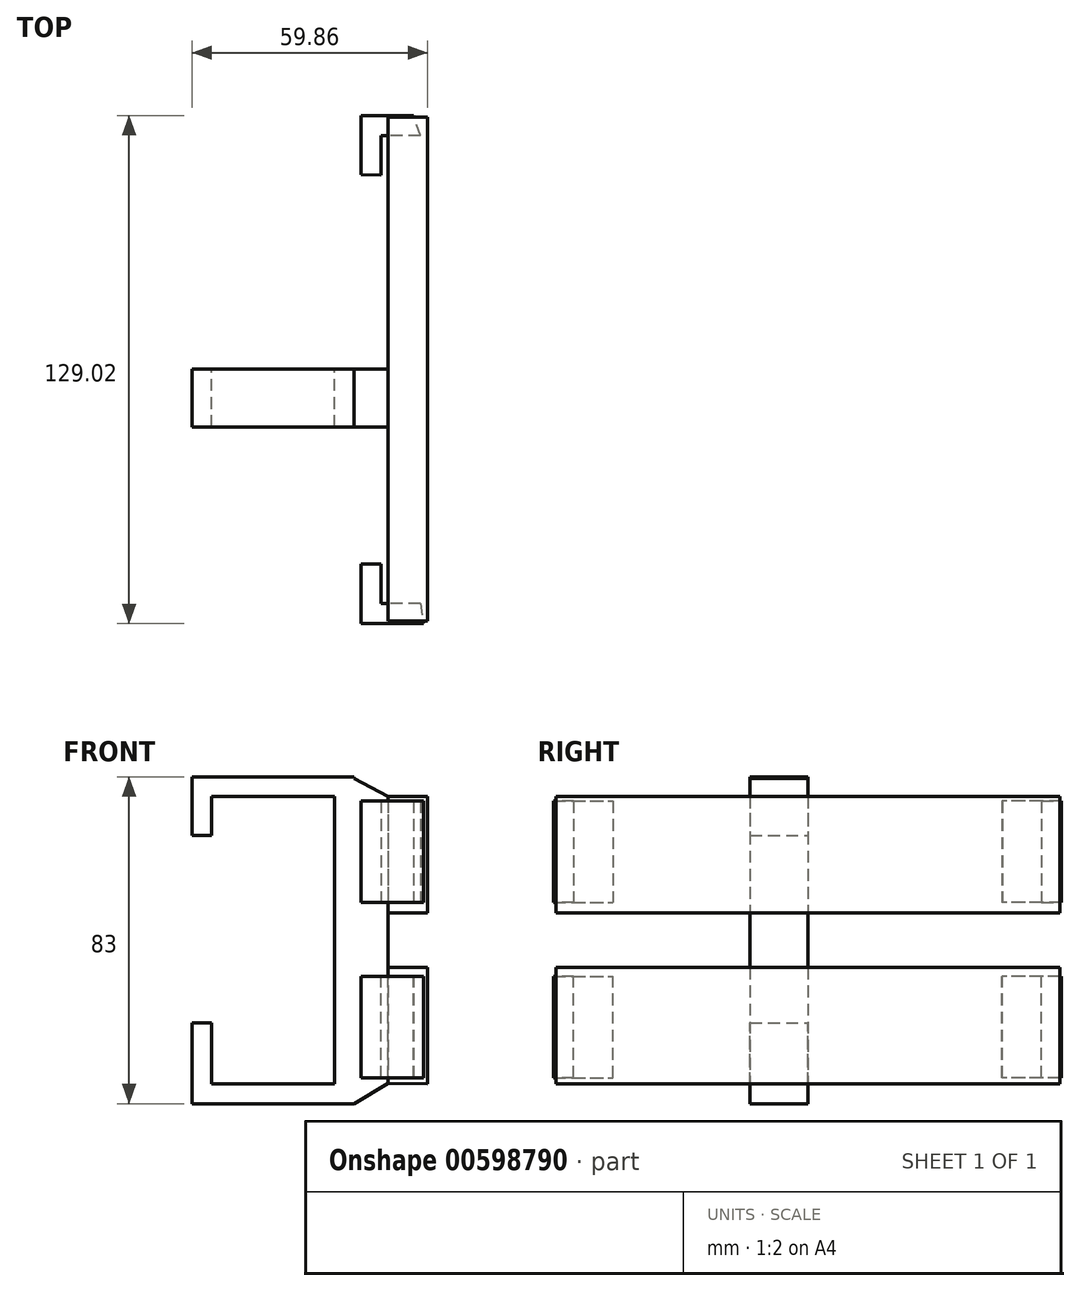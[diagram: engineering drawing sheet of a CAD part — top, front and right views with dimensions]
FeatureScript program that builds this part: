
annotation { "Feature Type Name" : "Feature", "Feature Type Description" : "" }
export const myFeature = defineFeature(function(context is Context, id is Id, definition is map)
    precondition{}
    {
        {
            var Q0;
            Q0=qCreatedBy(makeId("Front.planeOp"),FACE);
            var sketch = newSketch(context, id + "F0", { "sketchPlane" : qUnion([Q0])});
            skLineSegment(sketch, "E0", {"start": v(-93.76, -37.98) * mm, "end": v(-62.56, -37.98) * mm});
            skLineSegment(sketch, "E1", {"start": v(-62.56, -37.98) * mm, "end": v(-62.56, 35.02) * mm});
            skLineSegment(sketch, "E2", {"start": v(-62.56, 35.02) * mm, "end": v(-93.76, 35.02) * mm});
            skLineSegment(sketch, "E3", {"start": v(-93.76, 35.02) * mm, "end": v(-93.76, 25.22) * mm});
            skLineSegment(sketch, "E4", {"start": v(-93.76, -37.98) * mm, "end": v(-93.76, -22.48) * mm});
            skLineSegment(sketch, "E5.0", {"start": v(-98.76, 40.02) * mm, "end": v(-98.76, 25.22) * mm});
            skLineSegment(sketch, "E5.1", {"start": v(-98.76, -42.98) * mm, "end": v(-98.76, -22.48) * mm});
            skLineSegment(sketch, "E5.2", {"start": v(-98.76, -42.98) * mm, "end": v(-57.56, -42.98) * mm});
            skLineSegment(sketch, "E5.3", {"start": v(-57.56, -42.98) * mm, "end": v(-57.56, 40.02) * mm});
            skLineSegment(sketch, "E5.4", {"start": v(-57.56, 40.02) * mm, "end": v(-98.76, 40.02) * mm});
            skLineSegment(sketch, "E6", {"start": v(-93.76, 25.22) * mm, "end": v(-98.76, 25.22) * mm});
            skLineSegment(sketch, "E7", {"start": v(-93.76, -22.48) * mm, "end": v(-98.76, -22.48) * mm});
            skLineSegment(sketch, "E8", {"start": v(-57.56, 35.06) * mm, "end": v(-48.9, 35.06) * mm});
            skLineSegment(sketch, "E9", {"start": v(-48.9, 35.06) * mm, "end": v(-48.9, -37.87) * mm});
            skLineSegment(sketch, "E10", {"start": v(-48.9, -37.87) * mm, "end": v(-57.56, -37.87) * mm});
            skLineSegment(sketch, "E11", {"start": v(-57.94, 39.83) * mm, "end": v(-48.9, 35.06) * mm});
            skLineSegment(sketch, "E12", {"start": v(-48.9, -37.87) * mm, "end": v(-57.56, -42.98) * mm});
            skLineSegment(sketch, "E13", {"start": v(-38.9, 5.52) * mm, "end": v(-38.9, 35.02) * mm});
            skLineSegment(sketch, "E14", {"start": v(-38.9, 35.02) * mm, "end": v(-48.9, 35.06) * mm});
            skLineSegment(sketch, "E15", {"start": v(-48.9, -37.87) * mm, "end": v(-38.9, -37.9) * mm});
            skLineSegment(sketch, "E16", {"start": v(-38.9, -37.9) * mm, "end": v(-38.9, -8.4) * mm});
            skLineSegment(sketch, "E17", {"start": v(-38.9, -8.4) * mm, "end": v(-48.9, -8.37) * mm});
            skPoint(sketch, "E18.start.orphan", {"position": v(-38.9, 3.98) * mm});
            skLineSegment(sketch, "E19", {"start": v(-38.9, 5.52) * mm, "end": v(-48.9, 5.52) * mm});
            skSolve(sketch);
        }
        {
            var Q0;
            {var subQ2=sQuery(id+"F0.wireOp",EDGE,"E10");Q0=makeQuery(id+"F0.imprint","IMPRINT",FACE,{"disambiguationData":[TD([[makeQuery(id+"F0.imprint","IMPRINT",EDGE,{"derivedFrom":subQ2}),1.0]])]});}
            var Q1;
            {var subQ0=sQuery(id+"F0.wireOp",EDGE,"E8");Q1=makeQuery(id+"F0.imprint","IMPRINT",FACE,{"disambiguationData":[TD([[makeQuery(id+"F0.imprint","IMPRINT",EDGE,{"derivedFrom":subQ0}),1.0]])]});}
            var Q2;
            Q2=makeQuery(id+"F0.imprint","IMPRINT",FACE,{"disambiguationData":[TD([[makeQuery(id+"F0.imprint","IMPRINT",EDGE,{"derivedFrom":sQuery(id+"F0.wireOp",EDGE,"E0")}),-1.0]])]});
            var Q3;
            {var subQ3=sQuery(id+"F0.wireOp",EDGE,"E8");Q3=makeQuery(id+"F0.imprint","IMPRINT",FACE,{"disambiguationData":[TD([[makeQuery(id+"F0.imprint","IMPRINT",EDGE,{"derivedFrom":subQ3}),-1.0]])]});}
            extrude(context, id + "F1", {"entities" : qUnion([Q0, Q1, Q2, Q3]), "depth" : 14.7 * mm, "offsetDistance" : 25 * mm});
        }
        {
            var Q0;
            {var subQ0=sQuery(id+"F0.wireOp",EDGE,"E15");Q0=makeQuery(id+"F0.imprint","IMPRINT",FACE,{"disambiguationData":[TD([[makeQuery(id+"F0.imprint","IMPRINT",EDGE,{"derivedFrom":subQ0}),1.0]])]});}
            var Q1;
            Q1=makeQuery(id+"F0.imprint","IMPRINT",FACE,{"disambiguationData":[TD([[makeQuery(id+"F0.imprint","IMPRINT",EDGE,{"derivedFrom":sQuery(id+"F0.wireOp",EDGE,"E13")}),1.0]])]});
            extrude(context, id + "F2", {"entities" : qUnion([Q0, Q1]), "operationType" : NewBodyOperationType.ADD, "endBound" : BoundingType.SYMMETRIC, "depth" : 128 * mm, "offsetDistance" : 25 * mm});
        }
        {
            var Q0;
            Q0=qCreatedBy(makeId("Top.planeOp"),FACE);
            var sketch = newSketch(context, id + "F3", { "sketchPlane" : qUnion([Q0])});
            skLineSegment(sketch, "E20", {"start": v(-40.71, -59.52) * mm, "end": v(-50.71, -59.52) * mm});
            skLineSegment(sketch, "E21", {"start": v(-40.71, 59.3) * mm, "end": v(-50.71, 59.3) * mm});
            skLineSegment(sketch, "E22", {"start": v(-50.71, -59.52) * mm, "end": v(-50.71, -49.52) * mm});
            skLineSegment(sketch, "E23", {"start": v(-50.71, 59.3) * mm, "end": v(-50.71, 49.3) * mm});
            skLineSegment(sketch, "E24.0", {"start": v(-55.81, -64.62) * mm, "end": v(-55.81, -49.52) * mm});
            skLineSegment(sketch, "E24.1", {"start": v(-39.94, -64.62) * mm, "end": v(-55.81, -64.62) * mm});
            skLineSegment(sketch, "E25.0", {"start": v(-55.81, 64.4) * mm, "end": v(-55.81, 49.4) * mm});
            skLineSegment(sketch, "E25.1", {"start": v(-42.52, 64.4) * mm, "end": v(-55.81, 64.4) * mm});
            skLineSegment(sketch, "E26", {"start": v(-55.81, 49.4) * mm, "end": v(-50.71, 49.3) * mm});
            skLineSegment(sketch, "E27", {"start": v(-40.71, 59.3) * mm, "end": v(-42.52, 64.4) * mm});
            skLineSegment(sketch, "E28", {"start": v(-40.71, -59.52) * mm, "end": v(-39.94, -64.62) * mm});
            skLineSegment(sketch, "E29", {"start": v(-50.71, -49.52) * mm, "end": v(-55.81, -49.52) * mm});
            skSolve(sketch);
        }
        {
            var Q0;
            Q0=makeQuery(id+"F3.imprint","IMPRINT",FACE,{"disambiguationData":[TD([[makeQuery(id+"F3.imprint","IMPRINT",EDGE,{"derivedFrom":sQuery(id+"F3.wireOp",EDGE,"E21")}),-1.0]])]});
            var Q1;
            Q1=makeQuery(id+"F3.imprint","IMPRINT",FACE,{"disambiguationData":[TD([[makeQuery(id+"F3.imprint","IMPRINT",EDGE,{"derivedFrom":sQuery(id+"F3.wireOp",EDGE,"E20")}),1.0]])]});
            extrude(context, id + "F4", {"entities" : qUnion([Q0, Q1]), "depth" : 33.9 * mm, "offsetDistance" : 25 * mm, "hasSecondDirection" : true, "secondDirectionOppositeDirection" : false, "secondDirectionDepth" : 8.1 * mm});
        }
        {
            var Q0;
            Q0 = qSketchRegion(id + "F3", true);
            extrude(context, id + "F5", {"entities" : qUnion([Q0]), "operationType" : NewBodyOperationType.ADD, "oppositeDirection" : true, "depth" : 36.4 * mm, "offsetDistance" : 25 * mm, "hasSecondDirection" : true, "secondDirectionOppositeDirection" : true, "secondDirectionDepth" : 10.7 * mm});
        }
    });
